# Revit family: Single-Interior
name_source: partatom
category: Doors
revit_build: Autodesk Revit 2017 (Build: 20160225_1515(x64)
units: mm (PartAtom-declared; Revit-internal decimal feet)

## family parameters
Always vertical = Yes
Cut with Voids When Loaded = No
Host = Wall
Room Calculation Point = No
Shared = No

## types (6) — shared parameters
Analytic Construction = <None>
Assembly Code = C1020
Description = HINGED - SINGLE - INTERIOR
Door Finish = <By Category>
Door Hardware (Material) = <By Category>
Door Panel Style = Panel 2
Door Thickness = 0' - 1 3/8"
Fire Rating = --
Frame Finish = <By Category>
Frame Thickness = 0' - 1"
Function = Interior
Manufacturer = --
Model = --
Thickness = 0' - 1 3/8"
Trim ON/OFF = Yes
Wall Closure = By host

## per-type parameters (varying)
| type | Height | Width |
| 2-4x8-0 | 8' - 0" | 2' - 4" |
| 2-6x8-0 | 8' - 0" | 2' - 6" |
| 2-8x6-8 | 6' - 8" | 2' - 8" |
| 2-4x6-8 | 6' - 8" | 2' - 4" |
| 2-6x6-8 | 6' - 8" | 2' - 6" |
| 2-8x8-0 | 8' - 0" | 2' - 8" |

## geometry (parser evidence)
native form markers: Blend x8, Sweep x30
no freeform markers — native parametric forms only
